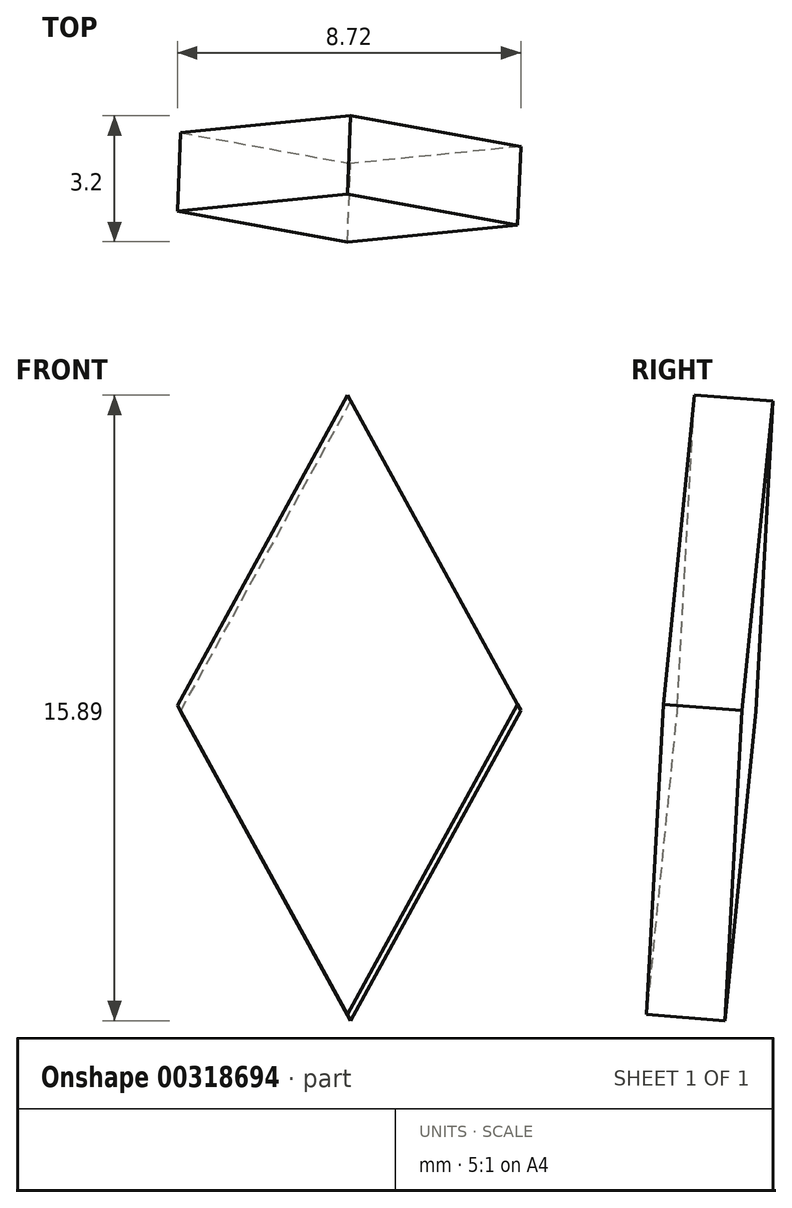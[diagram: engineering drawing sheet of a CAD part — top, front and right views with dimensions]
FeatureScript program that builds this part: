
annotation { "Feature Type Name" : "Feature", "Feature Type Description" : "" }
export const myFeature = defineFeature(function(context is Context, id is Id, definition is map)
    precondition{}
    {
        {
            var Q0;
            Q0=qCreatedBy(makeId("Front.planeOp"),FACE);
            var sketch = newSketch(context, id + "F0", { "sketchPlane" : qUnion([Q0])});
            skLineSegment(sketch, "E0", {"start": v(0, 0) * mm, "end": v(5.16, -2.74) * mm});
            skLineSegment(sketch, "E1", {"start": v(0, 0) * mm, "end": v(27.59, 0) * mm, "construction": true});
            skLineSegment(sketch, "E2.MirrorCS", {"start": v(0, 0) * mm, "end": v(5.16, 2.74) * mm});
            skLineSegment(sketch, "E3", {"start": v(5.16, 2.74) * mm, "end": v(5.16, -9.27) * mm, "construction": true});
            skLineSegment(sketch, "E4.MirrorCS", {"start": v(10.32, 0) * mm, "end": v(5.16, -2.74) * mm});
            skLineSegment(sketch, "E5.MirrorCS", {"start": v(10.32, 0) * mm, "end": v(5.16, 2.74) * mm});
            skSolve(sketch);
        }
        {
            var Q0;
            Q0 = qSketchRegion(id + "F0", true);
            extrude(context, id + "F1", {"entities" : qUnion([Q0]), "depth" : 2 * mm});
        }
        {
            var Q0;
            Q0=qCreatedBy(makeId("Front.planeOp"),FACE);
            cPlane(context, id + "F2", {"entities" : qUnion([Q0]), "cplaneType" : CPlaneType.OFFSET, "offset" : 50 * mm, "width" : 150 * mm, "height" : 150 * mm});
        }
        {
            var Q0;
            Q0=qCreatedBy(id+"F2.planeOp",FACE);
            var Q1;
            Q1=makeQuery(id+"F1.opExtrude","CAP_EDGE",EDGE,{"disambiguationData":[OSD([sQuery(id+"F0.wireOp",EDGE,"E4.MirrorCS")])],"isStart":false});
            cPlane(context, id + "F3", {"entities" : qUnion([Q0, Q1]), "cplaneType" : CPlaneType.LINE_ANGLE, "offset" : 25 * mm, "angle" : 5 * degree, "width" : 150 * mm, "height" : 150 * mm});
        }
        {
            var Q0;
            Q0=qCreatedBy(id+"F3.planeOp",FACE);
            cPlane(context, id + "F4", {"entities" : qUnion([Q0]), "cplaneType" : CPlaneType.OFFSET, "offset" : 50 * mm, "oppositeDirection" : true, "width" : 150 * mm, "height" : 150 * mm});
        }
        {
            var Q0;
            Q0=qCreatedBy(id+"F4.planeOp",FACE);
            var sketch = newSketch(context, id + "F5", { "sketchPlane" : qUnion([Q0])});
            skLineSegment(sketch, "E6", {"start": v(-4.33, 0) * mm, "end": v(4.33, 0) * mm, "construction": true});
            skLineSegment(sketch, "E7", {"start": v(0, 0) * mm, "end": v(0, -15.78) * mm, "construction": true});
            skLineSegment(sketch, "E8", {"start": v(-4.33, 0) * mm, "end": v(0, -7.9) * mm});
            skLineSegment(sketch, "E9.MirrorCS", {"start": v(4.33, 0) * mm, "end": v(-4.33, 0) * mm, "construction": true});
            skLineSegment(sketch, "E10.MirrorCS", {"start": v(4.33, 0) * mm, "end": v(0, -7.9) * mm});
            skLineSegment(sketch, "E11.MirrorCS", {"start": v(4.33, 0) * mm, "end": v(0, 7.9) * mm});
            skLineSegment(sketch, "E12.MirrorCS", {"start": v(-4.33, 0) * mm, "end": v(0, 7.9) * mm});
            skSolve(sketch);
        }
        {
            var Q0;
            Q0 = qSketchRegion(id + "F5", true);
            extrude(context, id + "F6", {"entities" : qUnion([Q0]), "oppositeDirection" : true, "depth" : 2 * mm});
        }
        {
            var Q0;
            Q0=makeQuery(id+"F1.opExtrude","SWEPT_BODY",BODY,{"disambiguationData":[OSD([sQuery(id+"F0.wireOp",EDGE,"E0"),sQuery(id+"F0.wireOp",EDGE,"E2.MirrorCS"),sQuery(id+"F0.wireOp",EDGE,"E4.MirrorCS"),sQuery(id+"F0.wireOp",EDGE,"E5.MirrorCS")])]});
            deleteBodies(context, id + "F7", {"entities" : qUnion([Q0])});
        }
    });
